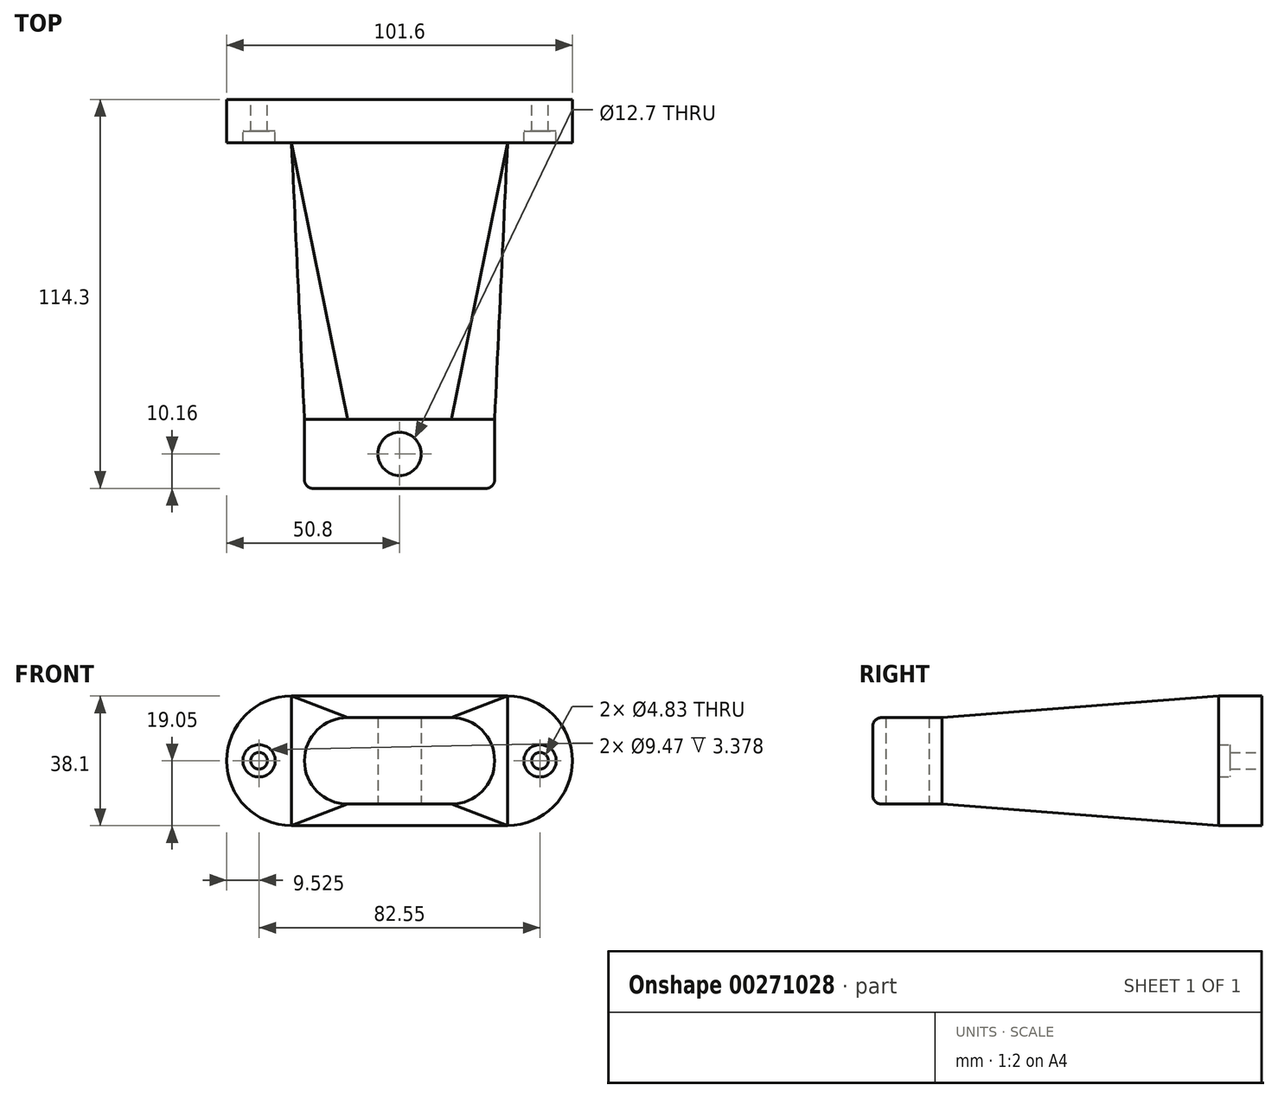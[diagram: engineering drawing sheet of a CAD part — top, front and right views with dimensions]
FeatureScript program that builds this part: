
annotation { "Feature Type Name" : "Feature", "Feature Type Description" : "" }
export const myFeature = defineFeature(function(context is Context, id is Id, definition is map)
    precondition{}
    {
        {
            var Q0;
            Q0=qCreatedBy(makeId("Front.planeOp"),FACE);
            var sketch = newSketch(context, id + "F0", { "sketchPlane" : qUnion([Q0])});
            skLineSegment(sketch, "E0.bottom", {"start": v(19.05, 0) * mm, "end": v(82.55, 0) * mm});
            skLineSegment(sketch, "E0.top", {"start": v(19.05, 38.1) * mm, "end": v(82.55, 38.1) * mm});
            skLineSegment(sketch, "E0.left", {"start": v(0, 19.05) * mm, "end": v(0, 19.05) * mm});
            skLineSegment(sketch, "E0.right", {"start": v(101.6, 19.05) * mm, "end": v(101.6, 19.05) * mm});
            skPoint(sketch, "E1.visualSharp", {"position": v(0, 38.1) * mm});
            skArc(sketch, "E1.filletArc", {"start": v(19.05, 38.1) * mm, "mid": v(5.58, 32.52) * mm, "end": v(0, 19.05) * mm});
            skPoint(sketch, "E2.visualSharp", {"position": v(101.6, 38.1) * mm});
            skArc(sketch, "E2.filletArc", {"start": v(101.6, 19.05) * mm, "mid": v(96.02, 32.52) * mm, "end": v(82.55, 38.1) * mm});
            skPoint(sketch, "E3.visualSharp", {"position": v(0, 0) * mm});
            skArc(sketch, "E3.filletArc", {"start": v(0, 19.05) * mm, "mid": v(5.58, 5.58) * mm, "end": v(19.05, 0) * mm});
            skPoint(sketch, "E4.visualSharp", {"position": v(101.6, 0) * mm});
            skArc(sketch, "E4.filletArc", {"start": v(82.55, 0) * mm, "mid": v(96.02, 5.58) * mm, "end": v(101.6, 19.05) * mm});
            skSolve(sketch);
        }
        {
            var Q0;
            Q0 = qSketchRegion(id + "F0", true);
            extrude(context, id + "F1", {"entities" : qUnion([Q0]), "depth" : 12.7 * mm});
        }
        {
            var Q0;
            Q0=makeQuery(id+"F1.opExtrude","CAP_FACE",FACE,{"disambiguationData":[OSD([sQuery(id+"F0.wireOp",EDGE,"E0.bottom"),sQuery(id+"F0.wireOp",EDGE,"E0.top"),sQuery(id+"F0.wireOp",EDGE,"E1.filletArc"),sQuery(id+"F0.wireOp",EDGE,"E2.filletArc"),sQuery(id+"F0.wireOp",EDGE,"E3.filletArc"),sQuery(id+"F0.wireOp",EDGE,"E4.filletArc")])],"isStart":false});
            cPlane(context, id + "F2", {"entities" : qUnion([Q0]), "cplaneType" : CPlaneType.OFFSET, "offset" : 81.28 * mm, "width" : 152.4 * mm, "height" : 152.4 * mm});
        }
        {
            var Q0;
            Q0=qCreatedBy(id+"F2.planeOp",FACE);
            var sketch = newSketch(context, id + "F3", { "sketchPlane" : qUnion([Q0])});
            skLineSegment(sketch, "E5.bottom", {"start": v(35.56, 6.35) * mm, "end": v(66.04, 6.35) * mm});
            skLineSegment(sketch, "E5.top", {"start": v(35.56, 31.75) * mm, "end": v(66.04, 31.75) * mm});
            skLineSegment(sketch, "E5.left", {"start": v(22.86, 19.05) * mm, "end": v(22.86, 19.05) * mm});
            skLineSegment(sketch, "E5.right", {"start": v(78.74, 19.05) * mm, "end": v(78.74, 19.05) * mm});
            skPoint(sketch, "E6.visualSharp", {"position": v(22.86, 31.75) * mm});
            skArc(sketch, "E6.filletArc", {"start": v(35.56, 31.75) * mm, "mid": v(26.58, 28.03) * mm, "end": v(22.86, 19.05) * mm});
            skPoint(sketch, "E7.visualSharp", {"position": v(22.86, 6.35) * mm});
            skArc(sketch, "E7.filletArc", {"start": v(22.86, 19.05) * mm, "mid": v(26.58, 10.07) * mm, "end": v(35.56, 6.35) * mm});
            skPoint(sketch, "E8.visualSharp", {"position": v(78.74, 31.75) * mm});
            skArc(sketch, "E8.filletArc", {"start": v(78.74, 19.05) * mm, "mid": v(75.02, 28.03) * mm, "end": v(66.04, 31.75) * mm});
            skPoint(sketch, "E9.visualSharp", {"position": v(78.74, 6.35) * mm});
            skArc(sketch, "E9.filletArc", {"start": v(66.04, 6.35) * mm, "mid": v(75.02, 10.07) * mm, "end": v(78.74, 19.05) * mm});
            skPoint(sketch, "E10.0.center.orphan", {"position": v(12.7, 12.7) * mm});
            skPoint(sketch, "E10.0.start.orphan", {"position": v(19.05, 38.1) * mm});
            skPoint(sketch, "E11.0.start.orphan", {"position": v(19.05, 0) * mm});
            skPoint(sketch, "E12.0.end.orphan", {"position": v(82.55, 38.1) * mm});
            skPoint(sketch, "E12.0.start.orphan", {"position": v(82.55, 0) * mm});
            skSolve(sketch);
        }
        {
            var Q0;
            Q0=makeQuery(id+"F1.opExtrude","CAP_FACE",FACE,{"disambiguationData":[OSD([sQuery(id+"F0.wireOp",EDGE,"E0.bottom"),sQuery(id+"F0.wireOp",EDGE,"E0.top"),sQuery(id+"F0.wireOp",EDGE,"E1.filletArc"),sQuery(id+"F0.wireOp",EDGE,"E2.filletArc"),sQuery(id+"F0.wireOp",EDGE,"E3.filletArc"),sQuery(id+"F0.wireOp",EDGE,"E4.filletArc")])],"isStart":false});
            var sketch = newSketch(context, id + "F4", { "sketchPlane" : qUnion([Q0])});
            skLineSegment(sketch, "E13.bottom", {"start": v(19.05, 0) * mm, "end": v(82.55, 0) * mm});
            skLineSegment(sketch, "E13.top", {"start": v(19.05, 38.1) * mm, "end": v(82.55, 38.1) * mm});
            skLineSegment(sketch, "E13.left", {"start": v(19.05, 0) * mm, "end": v(19.05, 38.1) * mm});
            skLineSegment(sketch, "E13.right", {"start": v(82.55, 0) * mm, "end": v(82.55, 38.1) * mm});
            skSolve(sketch);
        }
        {
            var Q0;
            Q0=makeQuery(id+"F3.imprint","IMPRINT",FACE,{"disambiguationData":[TD([[makeQuery(id+"F3.imprint","IMPRINT",EDGE,{"derivedFrom":sQuery(id+"F3.wireOp",EDGE,"E5.bottom")}),1.0]])]});
            extrude(context, id + "F5", {"entities" : qUnion([Q0]), "depth" : 20.32 * mm});
        }
        {
            var Q0;
            Q0=makeQuery(id+"F4.imprint","IMPRINT",FACE,{"disambiguationData":[TD([[makeQuery(id+"F4.imprint","IMPRINT",EDGE,{"derivedFrom":sQuery(id+"F4.wireOp",EDGE,"E13.bottom")}),1.0]])]});
            var Q1;
            Q1=makeQuery(id+"F5.opExtrude","CAP_FACE",FACE,{"disambiguationData":[OSD([sQuery(id+"F3.wireOp",EDGE,"E5.bottom"),sQuery(id+"F3.wireOp",EDGE,"E5.top"),sQuery(id+"F3.wireOp",EDGE,"E6.filletArc"),sQuery(id+"F3.wireOp",EDGE,"E7.filletArc"),sQuery(id+"F3.wireOp",EDGE,"E8.filletArc"),sQuery(id+"F3.wireOp",EDGE,"E9.filletArc")])],"isStart":true});
            loft(context, id + "F6", {"sheetProfilesArray" : [{ "sheetProfileEntities" : qUnion([Q0]) }, { "sheetProfileEntities" : qUnion([Q1]) }]});
        }
        {
            var Q0;
            Q0=makeQuery(id+"F1.opExtrude","SWEPT_BODY",BODY,{"disambiguationData":[OSD([sQuery(id+"F0.wireOp",EDGE,"E0.bottom"),sQuery(id+"F0.wireOp",EDGE,"E0.top"),sQuery(id+"F0.wireOp",EDGE,"E1.filletArc"),sQuery(id+"F0.wireOp",EDGE,"E2.filletArc"),sQuery(id+"F0.wireOp",EDGE,"E3.filletArc"),sQuery(id+"F0.wireOp",EDGE,"E4.filletArc")])]});
            var Q1;
            Q1=makeQuery(id+"F5.opExtrude","SWEPT_BODY",BODY,{"disambiguationData":[OSD([sQuery(id+"F3.wireOp",EDGE,"E5.bottom"),sQuery(id+"F3.wireOp",EDGE,"E5.top"),sQuery(id+"F3.wireOp",EDGE,"E6.filletArc"),sQuery(id+"F3.wireOp",EDGE,"E7.filletArc"),sQuery(id+"F3.wireOp",EDGE,"E8.filletArc"),sQuery(id+"F3.wireOp",EDGE,"E9.filletArc")])]});
            var Q2;
            Q2=makeQuery(id+"F6.opLoft","SWEPT_BODY",BODY,{"disambiguationData":[OSD([sQuery(id+"F3.wireOp",EDGE,"E5.bottom"),sQuery(id+"F3.wireOp",EDGE,"E5.top"),sQuery(id+"F3.wireOp",EDGE,"E6.filletArc"),sQuery(id+"F3.wireOp",EDGE,"E7.filletArc"),sQuery(id+"F3.wireOp",EDGE,"E8.filletArc"),sQuery(id+"F3.wireOp",EDGE,"E9.filletArc"),makeQuery(id+"F4.imprint","IMPRINT",FACE,{"disambiguationData":[TD([[makeQuery(id+"F4.imprint","IMPRINT",EDGE,{"derivedFrom":sQuery(id+"F4.wireOp",EDGE,"E13.bottom")}),1.0]])]})])]});
            booleanBodies(context, id + "F7", {"operationType" : BooleanOperationType.UNION, "tools" : qUnion([Q0, Q1, Q2])});
        }
        {
            var Q0;
            Q0=makeQuery(id+"F5.opExtrude","SWEPT_FACE",FACE,{"disambiguationData":[OSD([sQuery(id+"F3.wireOp",EDGE,"E5.top")])]});
            var sketch = newSketch(context, id + "F8", { "sketchPlane" : qUnion([Q0])});
            skPoint(sketch, "E14", {"position": v(50.8, -104.14) * mm});
            skPoint(sketch, "E14.positionSnap0", {"position": v(35.56, -104.14) * mm});
            skPoint(sketch, "E14.positionSnap1", {"position": v(50.8, -114.3) * mm});
            skSolve(sketch);
        }
        {
            var Q0;
            Q0=sQuery(id+"F8.wireOp",VERTEX,"E14");
            var Q1;
            Q1=makeQuery(id+"F1.opExtrude","SWEPT_BODY",BODY,{"disambiguationData":[OSD([sQuery(id+"F0.wireOp",EDGE,"E0.bottom"),sQuery(id+"F0.wireOp",EDGE,"E0.top"),sQuery(id+"F0.wireOp",EDGE,"E1.filletArc"),sQuery(id+"F0.wireOp",EDGE,"E2.filletArc"),sQuery(id+"F0.wireOp",EDGE,"E3.filletArc"),sQuery(id+"F0.wireOp",EDGE,"E4.filletArc")])]});
            hole(context, id + "F9", {"style" : HoleStyle.SIMPLE, "endStyle" : HoleEndStyle.THROUGH, "holeDiameter" : 12.7 * mm, "tappedDepth" : 12.7 * mm, "tapClearance" : 3, "locations" : qUnion([Q0]), "scope" : qUnion([Q1])});
        }
        {
            var Q0;
            {var subQ5=sQuery(id+"F0.wireOp",EDGE,"E4.filletArc");var subQ6=sQuery(id+"F0.wireOp",EDGE,"E3.filletArc");var subQ7=sQuery(id+"F0.wireOp",EDGE,"E2.filletArc");var subQ8=sQuery(id+"F0.wireOp",EDGE,"E1.filletArc");var subQ9=sQuery(id+"F0.wireOp",EDGE,"E0.top");var subQ10=sQuery(id+"F0.wireOp",EDGE,"E0.bottom");Q0=makeQuery(id+"F7.opBoolean","SPLIT",FACE,{"disambiguationData":[TD([makeQuery(id+"F1.opExtrude","SWEPT_FACE",FACE,{"disambiguationData":[OSD([subQ8,subQ6])]})])],"derivedFrom":makeQuery(id+"F1.opExtrude","CAP_FACE",FACE,{"disambiguationData":[OSD([subQ10,subQ9,subQ8,subQ7,subQ6,subQ5])],"isStart":false})});}
            var sketch = newSketch(context, id + "F10", { "sketchPlane" : qUnion([Q0])});
            skPoint(sketch, "E15", {"position": v(9.52, 19.05) * mm});
            skPoint(sketch, "E15.positionSnap0", {"position": v(0, 19.05) * mm});
            skPoint(sketch, "E16", {"position": v(92.08, 19.05) * mm});
            skSolve(sketch);
        }
        {
            var Q0;
            Q0=sQuery(id+"F10.wireOp",VERTEX,"E15");
            var Q1;
            Q1=sQuery(id+"F10.wireOp",VERTEX,"E16");
            var Q2;
            Q2=makeQuery(id+"F1.opExtrude","SWEPT_BODY",BODY,{"disambiguationData":[OSD([sQuery(id+"F0.wireOp",EDGE,"E0.bottom"),sQuery(id+"F0.wireOp",EDGE,"E0.top"),sQuery(id+"F0.wireOp",EDGE,"E1.filletArc"),sQuery(id+"F0.wireOp",EDGE,"E2.filletArc"),sQuery(id+"F0.wireOp",EDGE,"E3.filletArc"),sQuery(id+"F0.wireOp",EDGE,"E4.filletArc")])]});
            hole(context, id + "F11", {"style" : HoleStyle.C_BORE, "endStyle" : HoleEndStyle.THROUGH, "holeDiameter" : 4.83 * mm, "cBoreDiameter" : 9.47 * mm, "cBoreDepth" : 3.38 * mm, "tappedDepth" : 12.7 * mm, "tapClearance" : 3, "locations" : qUnion([Q0, Q1]), "scope" : qUnion([Q2])});
        }
        {
            var Q0;
            Q0=makeQuery(id+"F5.opExtrude","CAP_EDGE",EDGE,{"disambiguationData":[OSD([sQuery(id+"F3.wireOp",EDGE,"E5.top")])],"isStart":false});
            fillet(context, id + "F12", {"entities" : qUnion([Q0]), "radius" : 2.54 * mm, "tangentPropagation" : true, "allowEdgeOverflow" : false});
        }
    });
